# Revit family: Roxtec RS UG seals
name_source: partatom
category: Duct Accessories
revit_build: Autodesk Revit 2017 (Build: 20190508_0315(x64)
units: mm (PartAtom-declared; Revit-internal decimal feet)

## family parameters
Cut with Voids When Loaded = No
Host = Face
Part Type = Attaches To
Round Connector Dimension = Use Diameter
Shared = No

## types (10) — shared parameters
Core material = Roxylon black
Description = Sealing solutions for cables and pipes
ETIM Classification = EC000220
Fitting material = Steel
Fitting thickness = 5 mm  [stored 0.0164042 ft]
Frame material = Roxylon black
Manufacturer = Roxtec
Sealing height = 75 mm  [stored 0.246063 ft]
Sealing material = Roxylon black
URL = https://www.roxtec.com
Version = 2.0
zero-valued in all types: Default Elevation, NominalDepth, NominalHeight

## per-type parameters (varying)
| type | Front fitting diameter | LVI Numero | Max cable Ø | Min cable Ø | Sähkönumero | Wall opening diameter | Weight (kg) | core visibility |
| RS 100 24-53 UG | 110 mm  [stored 0.360892 ft] | - | 53 mm  [stored 0.173885 ft] | 24 mm  [stored 0.0787402 ft] | 1753126 | 100 mm  [stored 0.328084 ft] | 1 | Yes |
| RS 100 UG WOC | 110 mm  [stored 0.360892 ft] | 3259200 | 63 mm  [stored 0.206693 ft] | 39 mm  [stored 0.127953 ft] | 1753132 | 100 mm  [stored 0.328084 ft] | 1 | No |
| RS 125 UG WOC | 135 mm  [stored 0.442913 ft] | 3259201 | 88 mm  [stored 0.288714 ft] | 55 mm  [stored 0.180446 ft] | 1753187 | 125 mm  [stored 0.410105 ft] | 1.4 | No |
| RS 135 UG WOC | 145 mm  [stored 0.475722 ft] | - | 98 mm  [stored 0.321522 ft] | 65 mm  [stored 0.213255 ft] | 1753133 | 135 mm  [stored 0.442913 ft] | 1.6 | No |
| RS 150 UG WOC | 160 mm  [stored 0.524934 ft] | 3259202 | 113 mm  [stored 0.370735 ft] | 80 mm  [stored 0.262467 ft] |  | 150 mm  [stored 0.492126 ft] | 1.8 | No |
| RS 185 UG WOC | 195 mm  [stored 0.639764 ft] | 3259203 | 148 mm  [stored 0.485564 ft] | 114 mm  [stored 0.374016 ft] |  | 185 mm  [stored 0.606955 ft] | 2.3 | No |
| RS 75 UG | 85 mm  [stored 0.278871 ft] |  | 33 mm  [stored 0.108268 ft] | 9 mm  [stored 0.0295276 ft] | 1753091 | 75 mm  [stored 0.246063 ft] | 0.7 | Yes |
| RS 200 UG WOC | 210 mm  [stored 0.688976 ft] | 3259204 | 163 mm  [stored 0.534777 ft] | 130 mm  [stored 0.426509 ft] |  | 200 mm  [stored 0.656168 ft] | 2.5 | No |
| RS 225 UG WOC | 235 mm  [stored 0.770997 ft] | 3259205 | 179 mm  [stored 0.58727 ft] | 146 mm  [stored 0.479003 ft] |  | 225 mm  [stored 0.738189 ft] | 3.4 | No |
| RS 250 UG WOC | 260 mm  [stored 0.853018 ft] | 3259206 | 204 mm | 171 mm  [stored 0.561024 ft] |  | 250 mm  [stored 0.82021 ft] | 3.8 | No |

note: [stored X ft] marks values corroborated as IEEE doubles in the binary element streams (Revit-internal decimal feet)

## geometry (parser evidence)
native form markers: Sweep x3
no freeform markers — native parametric forms only
